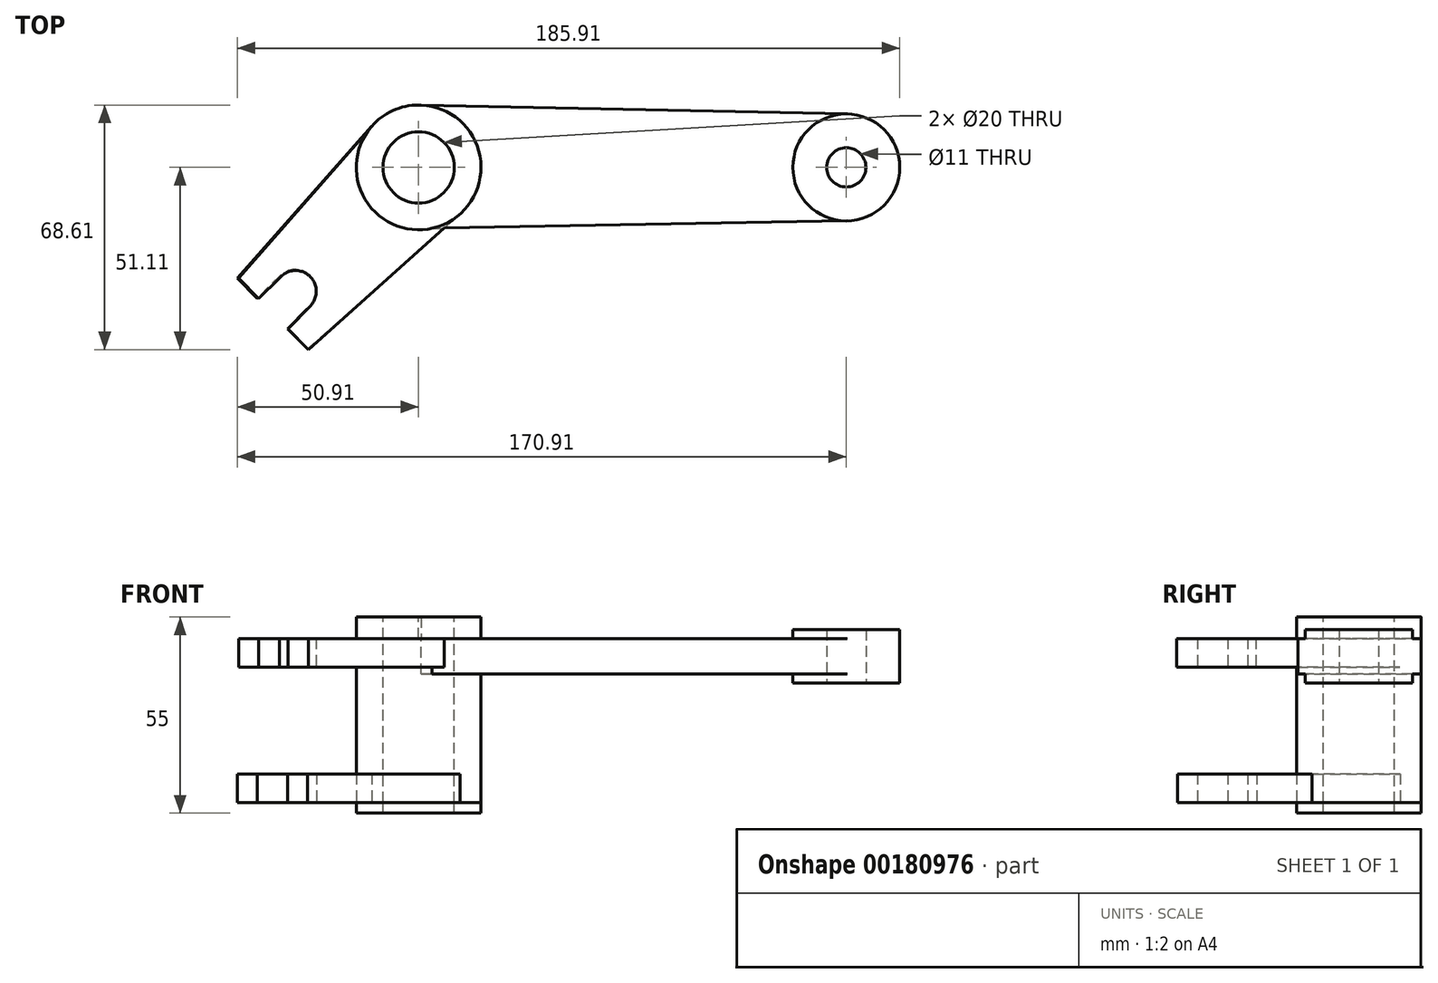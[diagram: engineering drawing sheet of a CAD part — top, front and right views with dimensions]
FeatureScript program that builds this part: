
annotation { "Feature Type Name" : "Feature", "Feature Type Description" : "" }
export const myFeature = defineFeature(function(context is Context, id is Id, definition is map)
    precondition{}
    {
        {
            var Q0;
            Q0=qCreatedBy(makeId("Top.planeOp"),FACE);
            var sketch = newSketch(context, id + "F0", { "sketchPlane" : qUnion([Q0])});
            skCircle(sketch, "E0", {"center": v(0, 0) * mm, "radius": 17.5 * mm});
            skSolve(sketch);
        }
        {
            var Q0;
            Q0 = qSketchRegion(id + "F0", true);
            extrude(context, id + "F1", {"entities" : qUnion([Q0]), "depth" : 3 * mm});
        }
        {
            var Q0;
            Q0=makeQuery(id+"F1.opExtrude","CAP_FACE",FACE,{"disambiguationData":[OSD([sQuery(id+"F0.wireOp",EDGE,"E0")])],"isStart":false});
            var sketch = newSketch(context, id + "F2", { "sketchPlane" : qUnion([Q0])});
            skLineSegment(sketch, "E1", {"start": v(0, 0) * mm, "end": v(133.12, 0) * mm});
            skLineSegment(sketch, "E2", {"start": v(-30.4, -30.4) * mm, "end": v(-34.65, -34.65) * mm});
            skLineSegment(sketch, "E3", {"start": v(0, 0) * mm, "end": v(-34.19, 34.19) * mm});
            skLineSegment(sketch, "E4.0", {"start": v(-31.11, -50.91) * mm, "end": v(-36.77, -45.25) * mm});
            skLineSegment(sketch, "E5", {"start": v(-50.91, -31.11) * mm, "end": v(-12.4, 12.4) * mm});
            skLineSegment(sketch, "E6", {"start": v(-31.11, -50.91) * mm, "end": v(11.6, -13.1) * mm});
            skArc(sketch, "E7", {"start": v(-30.4, -38.9) * mm, "mid": v(-30.4, -30.4) * mm, "end": v(-38.9, -30.4) * mm});
            skLineSegment(sketch, "E8", {"start": v(-38.9, -30.4) * mm, "end": v(-45.25, -36.77) * mm});
            skLineSegment(sketch, "E9", {"start": v(-30.4, -38.9) * mm, "end": v(-36.77, -45.25) * mm});
            skPoint(sketch, "E10.orphan", {"position": v(-44.55, -24.75) * mm});
            skLineSegment(sketch, "E11.trimOffspring", {"start": v(-45.25, -36.77) * mm, "end": v(-50.91, -31.11) * mm});
            skPoint(sketch, "E12.0.start.orphan", {"position": v(-24.75, -44.55) * mm});
            skSolve(sketch);
        }
        {
            var Q0;
            Q0 = qSketchRegion(id + "F2", true);
            var Q1;
            Q1=makeQuery(id+"F2.imprint","IMPRINT",FACE,{"disambiguationData":[TD([[makeQuery(id+"F2.imprint","IMPRINT",EDGE,{"derivedFrom":sQuery(id+"F2.wireOp",EDGE,"E4.0")}),-1.0]])]});
            extrude(context, id + "F3", {"entities" : qUnion([Q0, Q1]), "depth" : 25 * mm});
        }
        {
            var Q0;
            Q0=makeQuery(id+"F3.opExtrude","CAP_FACE",FACE,{"disambiguationData":[OSD([sQuery(id+"F0.wireOp",EDGE,"E0"),sQuery(id+"F2.wireOp",EDGE,"E4.0"),sQuery(id+"F2.wireOp",EDGE,"E5"),sQuery(id+"F2.wireOp",EDGE,"E6"),sQuery(id+"F2.wireOp",EDGE,"E7"),sQuery(id+"F2.wireOp",EDGE,"E8"),sQuery(id+"F2.wireOp",EDGE,"E9"),sQuery(id+"F2.wireOp",EDGE,"E11.trimOffspring")])],"isStart":false});
            extrude(context, id + "F4", {"entities" : qUnion([Q0]), "operationType" : NewBodyOperationType.REMOVE, "oppositeDirection" : true, "depth" : 17 * mm});
        }
        {
            var Q0;
            Q0=makeQuery(id+"F1.opExtrude","CAP_FACE",FACE,{"disambiguationData":[OSD([sQuery(id+"F0.wireOp",EDGE,"E0")])],"isStart":false});
            var sketch = newSketch(context, id + "F5", { "sketchPlane" : qUnion([Q0])});
            skCircle(sketch, "E13", {"center": v(0, 0) * mm, "radius": 17.5 * mm});
            skSolve(sketch);
        }
        {
            var Q0;
            Q0 = qSketchRegion(id + "F5", true);
            extrude(context, id + "F6", {"entities" : qUnion([Q0]), "depth" : 38 * mm});
        }
        {
            var Q0;
            Q0=makeQuery(id+"F6.opExtrude","CAP_FACE",FACE,{"disambiguationData":[OSD([sQuery(id+"F5.wireOp",EDGE,"E13")])],"isStart":false});
            var sketch = newSketch(context, id + "F7", { "sketchPlane" : qUnion([Q0])});
            skCircle(sketch, "E14", {"center": v(0, 0) * mm, "radius": 17.5 * mm});
            skLineSegment(sketch, "E15", {"start": v(-50.43, -31.12) * mm, "end": v(-13.18, 11.51) * mm});
            skLineSegment(sketch, "E16", {"start": v(-30.9, -51.11) * mm, "end": v(11.67, -13.04) * mm});
            skLineSegment(sketch, "E17", {"start": v(-50.43, -31.12) * mm, "end": v(-44.88, -36.8) * mm});
            skArc(sketch, "E18", {"start": v(-30.33, -38.78) * mm, "mid": v(-30.68, -30.36) * mm, "end": v(-39.07, -31.12) * mm});
            skLineSegment(sketch, "E19", {"start": v(-39.07, -31.12) * mm, "end": v(-44.88, -36.8) * mm});
            skLineSegment(sketch, "E20", {"start": v(-30.33, -38.78) * mm, "end": v(-36.6, -45.28) * mm});
            skLineSegment(sketch, "E21.trimOffspring", {"start": v(-36.6, -45.28) * mm, "end": v(-30.9, -51.11) * mm});
            skSolve(sketch);
        }
        {
            var Q0;
            Q0 = qSketchRegion(id + "F7", true);
            extrude(context, id + "F8", {"entities" : qUnion([Q0]), "operationType" : NewBodyOperationType.ADD, "depth" : 8 * mm});
        }
        {
            var Q0;
            Q0=makeQuery(id+"F8.opExtrude","CAP_FACE",FACE,{"disambiguationData":[OSD([sQuery(id+"F7.wireOp",EDGE,"E14"),sQuery(id+"F7.wireOp",EDGE,"E15"),sQuery(id+"F7.wireOp",EDGE,"E16"),sQuery(id+"F7.wireOp",EDGE,"E17"),sQuery(id+"F7.wireOp",EDGE,"E18"),sQuery(id+"F7.wireOp",EDGE,"E19"),sQuery(id+"F7.wireOp",EDGE,"E20"),sQuery(id+"F7.wireOp",EDGE,"E21.trimOffspring")])],"isStart":false});
            var sketch = newSketch(context, id + "F9", { "sketchPlane" : qUnion([Q0])});
            skCircle(sketch, "E22", {"center": v(120, 0) * mm, "radius": 15 * mm});
            skArc(sketch, "E23", {"start": v(3.77, -17.1) * mm, "mid": v(17.4, 1.9) * mm, "end": v(0, 17.5) * mm});
            skLineSegment(sketch, "E24", {"start": v(0, 17.5) * mm, "end": v(120.31, 15) * mm});
            skLineSegment(sketch, "E25", {"start": v(3.77, -17.1) * mm, "end": v(120.27, -15) * mm});
            skSolve(sketch);
        }
        {
            var Q0;
            Q0 = qSketchRegion(id + "F9", true);
            extrude(context, id + "F10", {"entities" : qUnion([Q0]), "operationType" : NewBodyOperationType.ADD, "oppositeDirection" : true, "depth" : 10 * mm});
        }
        {
            var Q0;
            Q0=makeQuery(id+"F10.boolean.opBoolean","MERGE",FACE,{"derivedFrom":[makeQuery(id+"F8.opExtrude","CAP_FACE",FACE,{"disambiguationData":[OSD([sQuery(id+"F7.wireOp",EDGE,"E14"),sQuery(id+"F7.wireOp",EDGE,"E15"),sQuery(id+"F7.wireOp",EDGE,"E16"),sQuery(id+"F7.wireOp",EDGE,"E17"),sQuery(id+"F7.wireOp",EDGE,"E18"),sQuery(id+"F7.wireOp",EDGE,"E19"),sQuery(id+"F7.wireOp",EDGE,"E20"),sQuery(id+"F7.wireOp",EDGE,"E21.trimOffspring")])],"isStart":false}),makeQuery(id+"F10.opExtrude","CAP_FACE",FACE,{"disambiguationData":[OSD([sQuery(id+"F9.wireOp",EDGE,"E22"),sQuery(id+"F9.wireOp",EDGE,"E23"),sQuery(id+"F9.wireOp",EDGE,"E24"),sQuery(id+"F9.wireOp",EDGE,"E25")])],"isStart":true})]});
            var sketch = newSketch(context, id + "F11", { "sketchPlane" : qUnion([Q0])});
            skCircle(sketch, "E26", {"center": v(0, 0) * mm, "radius": 17.5 * mm});
            skSolve(sketch);
        }
        {
            var Q0;
            Q0 = qSketchRegion(id + "F11", true);
            extrude(context, id + "F12", {"entities" : qUnion([Q0]), "operationType" : NewBodyOperationType.ADD, "depth" : 6 * mm});
        }
        {
            var Q0;
            Q0=makeQuery(id+"F12.opExtrude","CAP_FACE",FACE,{"disambiguationData":[OSD([sQuery(id+"F11.wireOp",EDGE,"E26")])],"isStart":false});
            var sketch = newSketch(context, id + "F13", { "sketchPlane" : qUnion([Q0])});
            skCircle(sketch, "E27", {"center": v(0, 0) * mm, "radius": 10 * mm});
            skSolve(sketch);
        }
        {
            var Q0;
            Q0=makeQuery(id+"F13.imprint","IMPRINT",FACE,{"disambiguationData":[TD([[makeQuery(id+"F13.imprint","IMPRINT",EDGE,{"derivedFrom":sQuery(id+"F13.wireOp",EDGE,"E27")}),1.0]])]});
            extrude(context, id + "F14", {"entities" : qUnion([Q0]), "operationType" : NewBodyOperationType.REMOVE, "oppositeDirection" : true, "depth" : 100 * mm});
        }
        {
            var Q0;
            Q0=makeQuery(id+"F10.boolean.opBoolean","MERGE",FACE,{"derivedFrom":[makeQuery(id+"F8.opExtrude","CAP_FACE",FACE,{"disambiguationData":[OSD([sQuery(id+"F7.wireOp",EDGE,"E14"),sQuery(id+"F7.wireOp",EDGE,"E15"),sQuery(id+"F7.wireOp",EDGE,"E16"),sQuery(id+"F7.wireOp",EDGE,"E17"),sQuery(id+"F7.wireOp",EDGE,"E18"),sQuery(id+"F7.wireOp",EDGE,"E19"),sQuery(id+"F7.wireOp",EDGE,"E20"),sQuery(id+"F7.wireOp",EDGE,"E21.trimOffspring")])],"isStart":false}),makeQuery(id+"F10.opExtrude","CAP_FACE",FACE,{"disambiguationData":[OSD([sQuery(id+"F9.wireOp",EDGE,"E22"),sQuery(id+"F9.wireOp",EDGE,"E23"),sQuery(id+"F9.wireOp",EDGE,"E24"),sQuery(id+"F9.wireOp",EDGE,"E25")])],"isStart":true})]});
            var sketch = newSketch(context, id + "F15", { "sketchPlane" : qUnion([Q0])});
            skCircle(sketch, "E28", {"center": v(120, 0) * mm, "radius": 15 * mm});
            skSolve(sketch);
        }
        {
            var Q0;
            Q0 = qSketchRegion(id + "F15", true);
            extrude(context, id + "F16", {"entities" : qUnion([Q0]), "operationType" : NewBodyOperationType.ADD, "depth" : 2.5 * mm});
        }
        {
            var Q0;
            Q0=makeQuery(id+"F10.opExtrude","CAP_FACE",FACE,{"disambiguationData":[OSD([sQuery(id+"F9.wireOp",EDGE,"E22"),sQuery(id+"F9.wireOp",EDGE,"E23"),sQuery(id+"F9.wireOp",EDGE,"E24"),sQuery(id+"F9.wireOp",EDGE,"E25")])],"isStart":false});
            var sketch = newSketch(context, id + "F17", { "sketchPlane" : qUnion([Q0])});
            skCircle(sketch, "E29", {"center": v(120, 0) * mm, "radius": 15 * mm});
            skSolve(sketch);
        }
        {
            var Q0;
            Q0 = qSketchRegion(id + "F17", true);
            extrude(context, id + "F18", {"entities" : qUnion([Q0]), "operationType" : NewBodyOperationType.ADD, "depth" : 2.5 * mm});
        }
        {
            var Q0;
            Q0=makeQuery(id+"F18.opExtrude","CAP_FACE",FACE,{"disambiguationData":[OSD([sQuery(id+"F17.wireOp",EDGE,"E29")])],"isStart":false});
            var sketch = newSketch(context, id + "F19", { "sketchPlane" : qUnion([Q0])});
            skCircle(sketch, "E30", {"center": v(120, 0) * mm, "radius": 5.5 * mm});
            skSolve(sketch);
        }
        {
            var Q0;
            Q0 = qSketchRegion(id + "F19", true);
            extrude(context, id + "F20", {"entities" : qUnion([Q0]), "operationType" : NewBodyOperationType.REMOVE, "oppositeDirection" : true, "depth" : 25 * mm});
        }
    });
